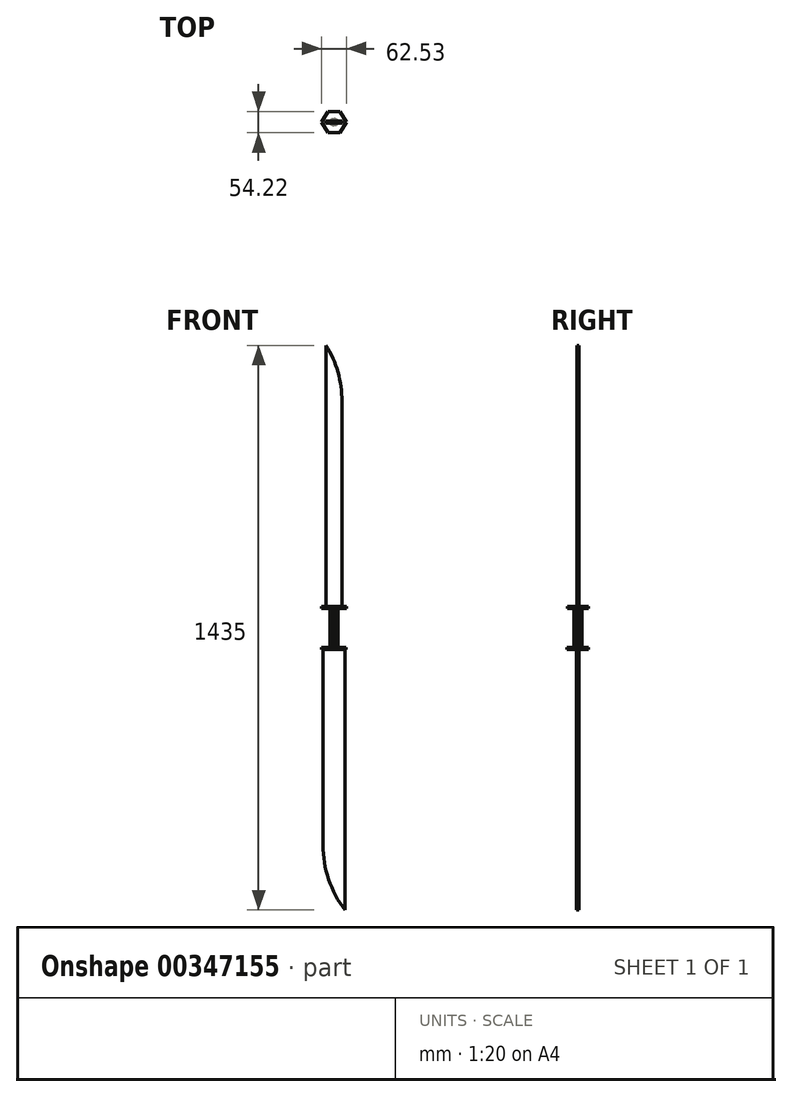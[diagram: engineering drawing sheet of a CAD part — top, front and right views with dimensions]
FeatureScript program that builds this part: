
annotation { "Feature Type Name" : "Feature", "Feature Type Description" : "" }
export const myFeature = defineFeature(function(context is Context, id is Id, definition is map)
    precondition{}
    {
        {
            var Q0;
            Q0=qCreatedBy(makeId("Top.planeOp"),FACE);
            var sketch = newSketch(context, id + "F0", { "sketchPlane" : qUnion([Q0])});
            skLineSegment(sketch, "E0.bottom", {"start": v(56.92, 4.85) * mm, "end": v(-56.92, 4.85) * mm});
            skLineSegment(sketch, "E0.top", {"start": v(56.92, -4.85) * mm, "end": v(-56.92, -4.85) * mm});
            skLineSegment(sketch, "E0.left", {"start": v(56.92, 4.85) * mm, "end": v(56.92, -4.85) * mm});
            skLineSegment(sketch, "E0.right", {"start": v(-56.92, 4.85) * mm, "end": v(-56.92, -4.85) * mm});
            skPoint(sketch, "E0.middle", {"position": v(0, 0) * mm});
            skLineSegment(sketch, "E1.bottom", {"start": v(20.15, -2.99) * mm, "end": v(-20.15, -2.99) * mm});
            skLineSegment(sketch, "E1.top", {"start": v(20.15, 2.99) * mm, "end": v(-20.15, 2.99) * mm});
            skLineSegment(sketch, "E1.left", {"start": v(20.15, -2.99) * mm, "end": v(20.15, 2.99) * mm});
            skLineSegment(sketch, "E1.right", {"start": v(-20.15, -2.99) * mm, "end": v(-20.15, 2.99) * mm});
            skSolve(sketch);
        }
        {
            var Q0;
            Q0=makeQuery(id+"F0.imprint","IMPRINT",FACE,{"disambiguationData":[TD([[makeQuery(id+"F0.imprint","IMPRINT",EDGE,{"derivedFrom":sQuery(id+"F0.wireOp",EDGE,"E1.bottom")}),-1.0]])]});
            extrude(context, id + "F1", {"entities" : qUnion([Q0]), "depth" : 668 * mm});
        }
        {
            var Q0;
            Q0=qCreatedBy(makeId("Top.planeOp"),FACE);
            var sketch = newSketch(context, id + "F2", { "sketchPlane" : qUnion([Q0])});
            skCircle(sketch, "E2.cCircle", {"center": v(0, 0) * mm, "radius": 9.86 * mm, "construction": true});
            skLineSegment(sketch, "E2.0", {"start": v(10.6, -1.3) * mm, "end": v(6.57, -8.4) * mm});
            skLineSegment(sketch, "E2.1", {"start": v(6.57, -8.4) * mm, "end": v(-1.3, -10.6) * mm});
            skLineSegment(sketch, "E2.2", {"start": v(-1.3, -10.6) * mm, "end": v(-8.4, -6.57) * mm});
            skLineSegment(sketch, "E2.3", {"start": v(-8.4, -6.57) * mm, "end": v(-10.6, 1.3) * mm});
            skLineSegment(sketch, "E2.4", {"start": v(-10.6, 1.3) * mm, "end": v(-6.57, 8.4) * mm});
            skLineSegment(sketch, "E2.5", {"start": v(-6.57, 8.4) * mm, "end": v(1.3, 10.6) * mm});
            skLineSegment(sketch, "E2.6", {"start": v(1.3, 10.6) * mm, "end": v(8.4, 6.57) * mm});
            skLineSegment(sketch, "E2.7", {"start": v(8.4, 6.57) * mm, "end": v(10.6, -1.3) * mm});
            skPoint(sketch, "E2.0.midPoint", {"position": v(8.58, -4.85) * mm});
            skSolve(sketch);
        }
        {
            var Q0;
            Q0=makeQuery(id+"F2.imprint","IMPRINT",FACE,{"disambiguationData":[TD([[makeQuery(id+"F2.imprint","IMPRINT",EDGE,{"derivedFrom":sQuery(id+"F2.wireOp",EDGE,"E2.0")}),-1.0]])]});
            extrude(context, id + "F3", {"entities" : qUnion([Q0]), "operationType" : NewBodyOperationType.ADD, "oppositeDirection" : true, "depth" : 100 * mm});
        }
        {
            var Q0;
            Q0=qCreatedBy(makeId("Top.planeOp"),FACE);
            var sketch = newSketch(context, id + "F4", { "sketchPlane" : qUnion([Q0])});
            skCircle(sketch, "E3.cCircle", {"center": v(0, 0) * mm, "radius": 27 * mm, "construction": true});
            skLineSegment(sketch, "E3.0", {"start": v(15.7, 26.93) * mm, "end": v(31.17, -0.14) * mm});
            skLineSegment(sketch, "E3.1", {"start": v(31.17, -0.14) * mm, "end": v(15.47, -27.06) * mm});
            skLineSegment(sketch, "E3.2", {"start": v(15.47, -27.06) * mm, "end": v(-15.7, -26.93) * mm});
            skLineSegment(sketch, "E3.3", {"start": v(-15.7, -26.93) * mm, "end": v(-31.17, 0.14) * mm});
            skLineSegment(sketch, "E3.4", {"start": v(-31.17, 0.14) * mm, "end": v(-15.47, 27.06) * mm});
            skLineSegment(sketch, "E3.5", {"start": v(-15.47, 27.06) * mm, "end": v(15.7, 26.93) * mm});
            skPoint(sketch, "E3.0.midPoint", {"position": v(23.44, 13.4) * mm});
            skSolve(sketch);
        }
        {
            var Q0;
            Q0=makeQuery(id+"F4.imprint","IMPRINT",FACE,{"disambiguationData":[TD([[makeQuery(id+"F4.imprint","IMPRINT",EDGE,{"derivedFrom":sQuery(id+"F4.wireOp",EDGE,"E3.0")}),-1.0]])]});
            extrude(context, id + "F5", {"entities" : qUnion([Q0]), "operationType" : NewBodyOperationType.ADD, "depth" : 5 * mm});
        }
        {
            var Q0;
            Q0=makeQuery(id+"F1.opExtrude","CAP_EDGE",EDGE,{"disambiguationData":[OSD([sQuery(id+"F0.wireOp",EDGE,"E1.left")])],"isStart":false});
            fillet(context, id + "F6", {"entities" : qUnion([Q0]), "radius" : 270.4 * mm, "tangentPropagation" : true, "allowEdgeOverflow" : false});
        }
        {
            var Q0;
            Q0=qCreatedBy(makeId("Top.planeOp"),FACE);
            cPlane(context, id + "F7", {"entities" : qUnion([Q0]), "cplaneType" : CPlaneType.OFFSET, "offset" : 99 * mm, "oppositeDirection" : true, "width" : 150 * mm, "height" : 150 * mm});
        }
        {
            var Q0;
            Q0=makeQuery(id+"F3.opExtrude","CAP_FACE",FACE,{"disambiguationData":[OSD([sQuery(id+"F2.wireOp",EDGE,"E2.0"),sQuery(id+"F2.wireOp",EDGE,"E2.1"),sQuery(id+"F2.wireOp",EDGE,"E2.2"),sQuery(id+"F2.wireOp",EDGE,"E2.3"),sQuery(id+"F2.wireOp",EDGE,"E2.4"),sQuery(id+"F2.wireOp",EDGE,"E2.5"),sQuery(id+"F2.wireOp",EDGE,"E2.6"),sQuery(id+"F2.wireOp",EDGE,"E2.7")])],"isStart":false});
            var sketch = newSketch(context, id + "F8", { "sketchPlane" : qUnion([Q0])});
            skCircle(sketch, "E4.cCircle", {"center": v(-0.2, 0.1) * mm, "radius": 27 * mm, "construction": true});
            skLineSegment(sketch, "E4.0", {"start": v(15.51, 27.03) * mm, "end": v(30.98, -0.04) * mm});
            skLineSegment(sketch, "E4.1", {"start": v(30.98, -0.04) * mm, "end": v(15.28, -26.96) * mm});
            skLineSegment(sketch, "E4.2", {"start": v(15.28, -26.96) * mm, "end": v(-15.9, -26.83) * mm});
            skLineSegment(sketch, "E4.3", {"start": v(-15.9, -26.83) * mm, "end": v(-31.36, 0.24) * mm});
            skLineSegment(sketch, "E4.4", {"start": v(-31.36, 0.24) * mm, "end": v(-15.66, 27.16) * mm});
            skLineSegment(sketch, "E4.5", {"start": v(-15.66, 27.16) * mm, "end": v(15.51, 27.03) * mm});
            skPoint(sketch, "E4.0.midPoint", {"position": v(23.25, 13.5) * mm});
            skSolve(sketch);
        }
        {
            var Q0;
            Q0=qSketchRegion(id+"F8",true);
            extrude(context, id + "F9", {"entities" : qUnion([Q0]), "operationType" : NewBodyOperationType.ADD, "depth" : 4.9 * mm});
        }
        {
            var Q0;
            Q0=qCreatedBy(id+"F7.planeOp",FACE);
            var sketch = newSketch(context, id + "F10", { "sketchPlane" : qUnion([Q0])});
            skLineSegment(sketch, "E5.bottom", {"start": v(28.1, 3.32) * mm, "end": v(-28.1, 3.32) * mm});
            skLineSegment(sketch, "E5.top", {"start": v(28.1, -3.32) * mm, "end": v(-28.1, -3.32) * mm});
            skLineSegment(sketch, "E5.left", {"start": v(28.1, 3.32) * mm, "end": v(28.1, -3.32) * mm});
            skLineSegment(sketch, "E5.right", {"start": v(-28.1, 3.32) * mm, "end": v(-28.1, -3.32) * mm});
            skPoint(sketch, "E5.middle", {"position": v(0, 0) * mm});
            skSolve(sketch);
        }
        {
            var Q0;
            Q0=qSketchRegion(id+"F10",true);
            extrude(context, id + "F11", {"entities" : qUnion([Q0]), "operationType" : NewBodyOperationType.ADD, "oppositeDirection" : true, "depth" : 668 * mm});
        }
        {
            var Q0;
            Q0=makeQuery(id+"F11.opExtrude","CAP_EDGE",EDGE,{"disambiguationData":[OSD([sQuery(id+"F10.wireOp",EDGE,"E5.right")])],"isStart":false});
            fillet(context, id + "F12", {"entities" : qUnion([Q0]), "radius" : 270.4 * mm, "tangentPropagation" : true, "allowEdgeOverflow" : false});
        }
    });
